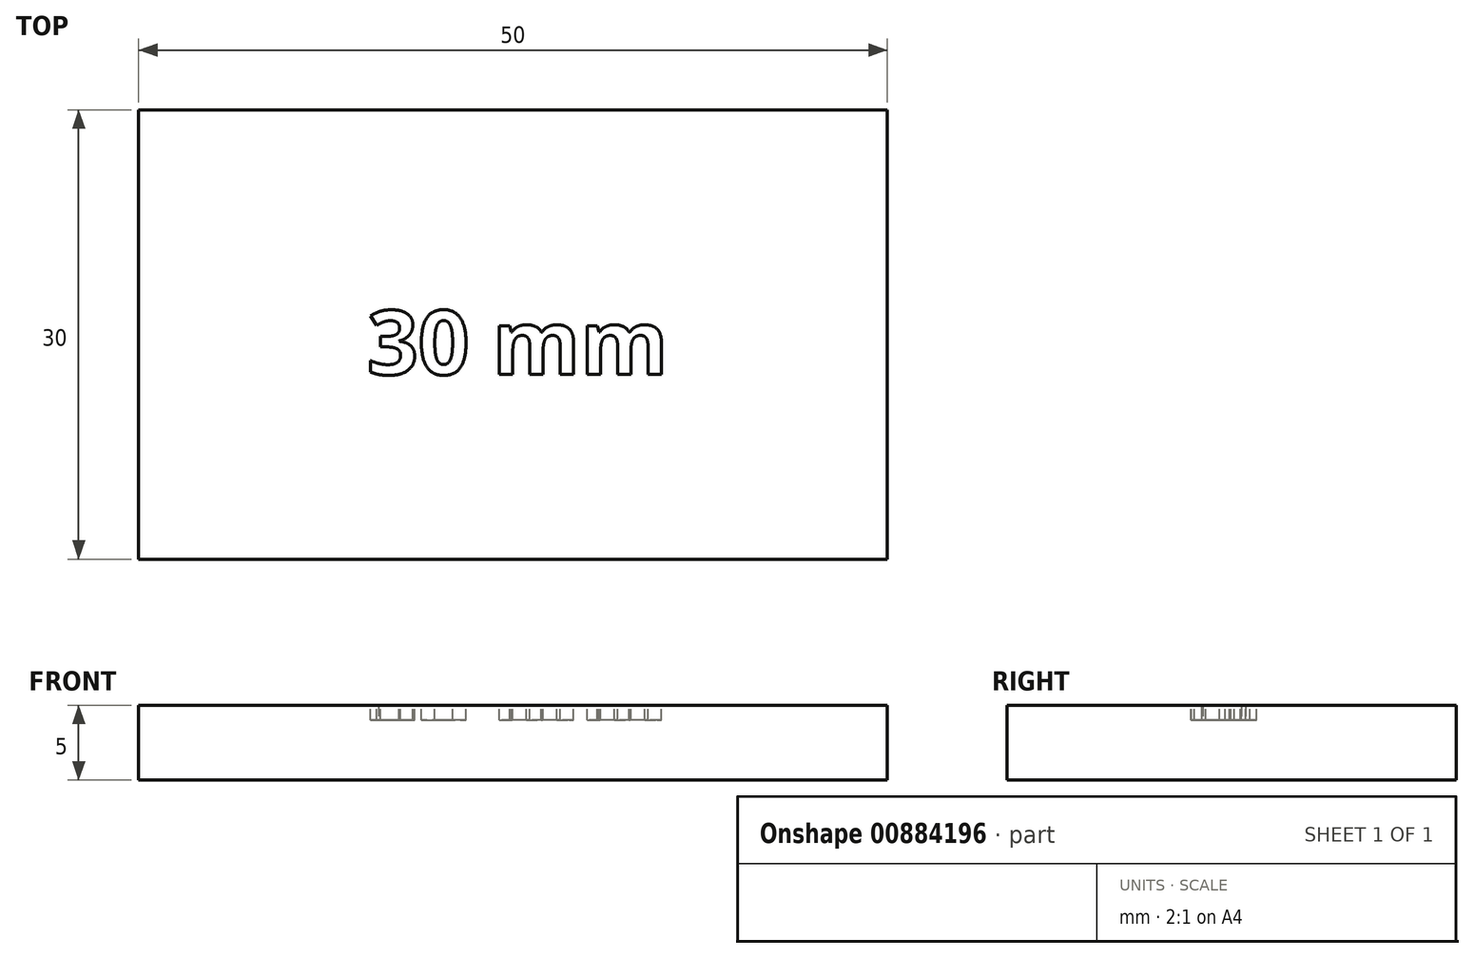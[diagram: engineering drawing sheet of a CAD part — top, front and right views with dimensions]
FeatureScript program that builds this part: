
annotation { "Feature Type Name" : "Feature", "Feature Type Description" : "" }
export const myFeature = defineFeature(function(context is Context, id is Id, definition is map)
    precondition{}
    {
        {
            var Q0;
            Q0=qCreatedBy(makeId("Top.planeOp"),FACE);
            var sketch = newSketch(context, id + "F0", { "sketchPlane" : qUnion([Q0])});
            skLineSegment(sketch, "E0.bottom", {"start": v(-50, 30) * mm, "end": v(0, 30) * mm});
            skLineSegment(sketch, "E0.top", {"start": v(-50, 0) * mm, "end": v(0, 0) * mm});
            skLineSegment(sketch, "E0.left", {"start": v(-50, 30) * mm, "end": v(-50, 0) * mm});
            skLineSegment(sketch, "E0.right", {"start": v(0, 30) * mm, "end": v(0, 0) * mm});
            skSolve(sketch);
        }
        {
            var Q0;
            Q0=makeQuery(id+"F0.imprint","IMPRINT",FACE,{"disambiguationData":[TD([[makeQuery(id+"F0.imprint","IMPRINT",EDGE,{"derivedFrom":sQuery(id+"F0.wireOp",EDGE,"E0.bottom")}),-1.0]])]});
            extrude(context, id + "F1", {"entities" : qUnion([Q0]), "depth" : 5 * mm, "offsetDistance" : 25 * mm});
        }
        {
            var Q0;
            Q0=makeQuery(id+"F1.opExtrude","CAP_FACE",FACE,{"disambiguationData":[OSD([sQuery(id+"F0.wireOp",EDGE,"E0.bottom"),sQuery(id+"F0.wireOp",EDGE,"E0.top"),sQuery(id+"F0.wireOp",EDGE,"E0.left"),sQuery(id+"F0.wireOp",EDGE,"E0.right")])],"isStart":false});
            var sketch = newSketch(context, id + "F2", { "sketchPlane" : qUnion([Q0])});
            skText(sketch, "E1", { "text": "30 mm", "fontName": "OpenSans-Bold.ttf"});
            const initialGuessF2  = {"E1": [-0.03474, 0.01233, 1, 0, 0.0043]};
            skSetInitialGuess(sketch, initialGuessF2);
            skSolve(sketch);
        }
        {
            var Q0;
            Q0 = qSketchRegion(id + "F2", true);
            extrude(context, id + "F3", {"entities" : qUnion([Q0]), "operationType" : NewBodyOperationType.REMOVE, "oppositeDirection" : true, "depth" : 1 * mm, "offsetDistance" : 25 * mm});
        }
    });
